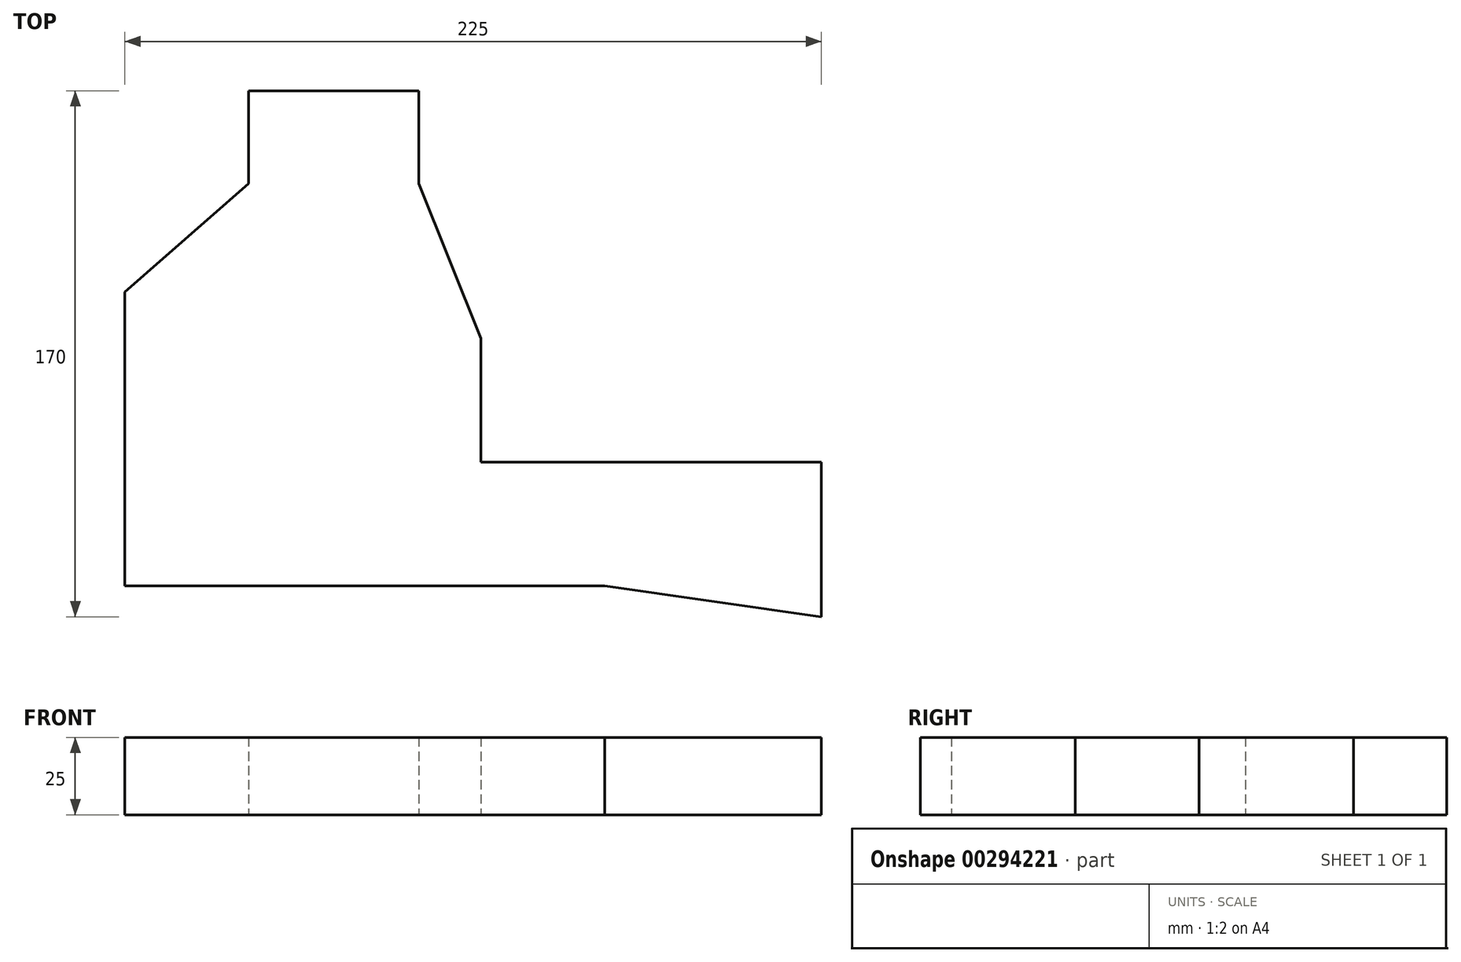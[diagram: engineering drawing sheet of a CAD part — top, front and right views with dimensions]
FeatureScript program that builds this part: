
annotation { "Feature Type Name" : "Feature", "Feature Type Description" : "" }
export const myFeature = defineFeature(function(context is Context, id is Id, definition is map)
    precondition{}
    {
        {
            var Q0;
            Q0=qCreatedBy(makeId("Top.planeOp"),FACE);
            var sketch = newSketch(context, id + "F0", { "sketchPlane" : qUnion([Q0])});
            skLineSegment(sketch, "E0", {"start": v(-221.63, -19.93) * mm, "end": v(-221.63, -114.93) * mm});
            skLineSegment(sketch, "E1", {"start": v(-221.63, -114.93) * mm, "end": v(-66.63, -114.93) * mm});
            skLineSegment(sketch, "E2", {"start": v(-66.63, -114.93) * mm, "end": v(3.37, -124.93) * mm});
            skLineSegment(sketch, "E3", {"start": v(3.37, -74.93) * mm, "end": v(3.37, -124.93) * mm});
            skLineSegment(sketch, "E4", {"start": v(3.37, -74.93) * mm, "end": v(-106.63, -74.93) * mm});
            skLineSegment(sketch, "E5", {"start": v(-106.63, -74.93) * mm, "end": v(-106.63, -34.93) * mm});
            skLineSegment(sketch, "E6", {"start": v(-106.63, -34.93) * mm, "end": v(-126.63, 15.07) * mm});
            skLineSegment(sketch, "E7", {"start": v(-126.63, 15.07) * mm, "end": v(-126.63, 45.07) * mm});
            skLineSegment(sketch, "E8", {"start": v(-126.63, 45.07) * mm, "end": v(-181.63, 45.07) * mm});
            skLineSegment(sketch, "E9", {"start": v(-181.63, 45.07) * mm, "end": v(-181.63, 15.07) * mm});
            skLineSegment(sketch, "E10", {"start": v(-181.63, 15.07) * mm, "end": v(-221.63, -19.93) * mm});
            skSolve(sketch);
        }
        {
            var Q0;
            Q0 = qSketchRegion(id + "F0", true);
            extrude(context, id + "F1", {"entities" : qUnion([Q0]), "depth" : 25 * mm});
        }
    });
